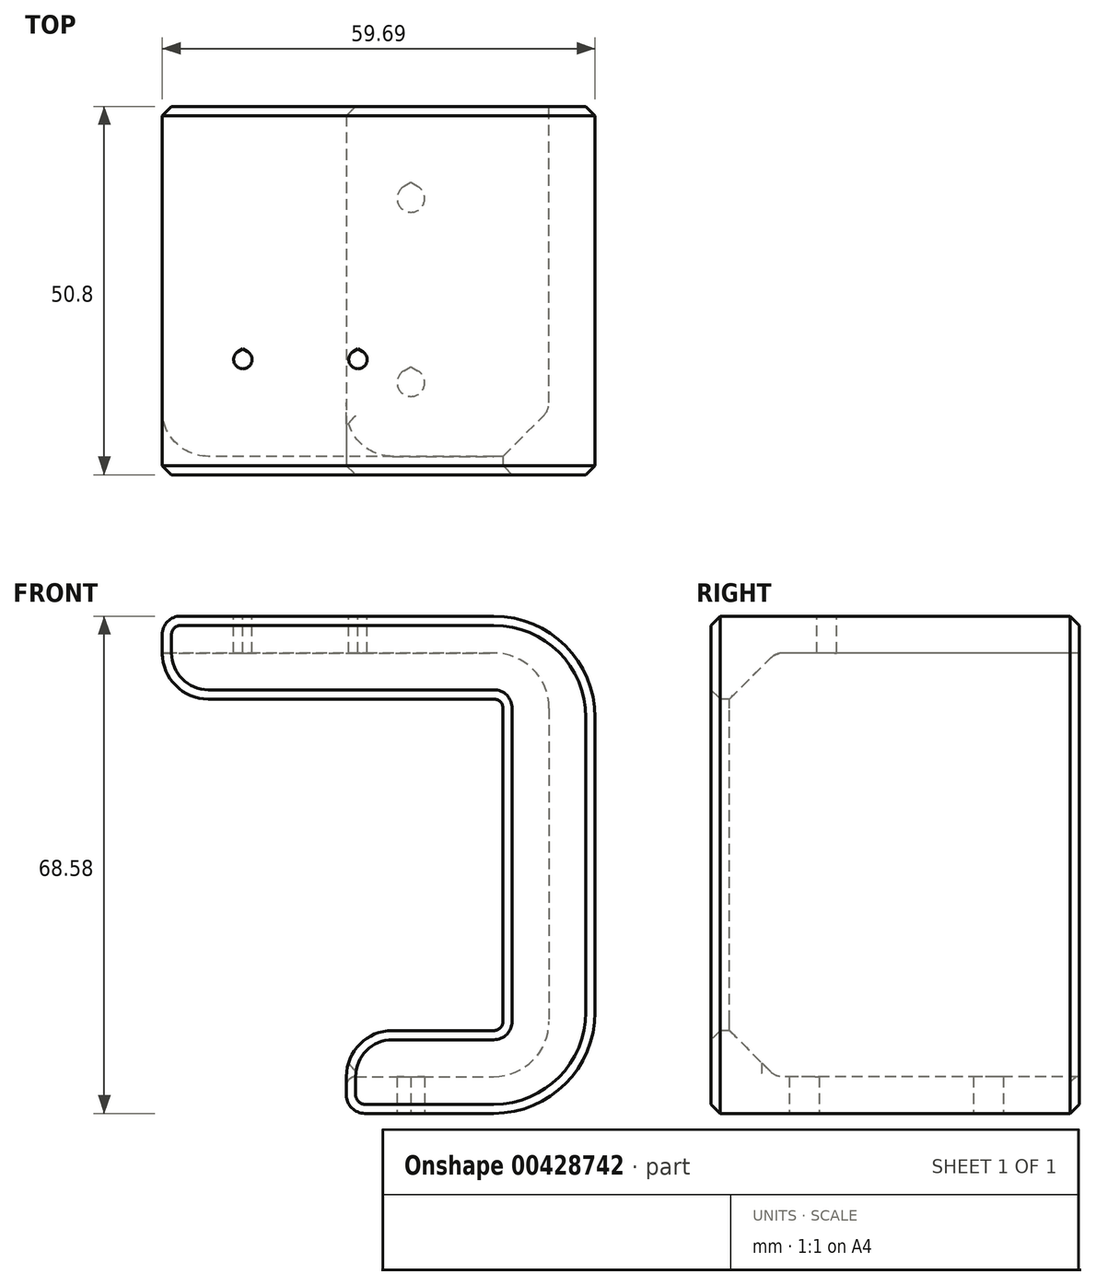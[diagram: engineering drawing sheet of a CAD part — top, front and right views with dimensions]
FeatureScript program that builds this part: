
annotation { "Feature Type Name" : "Feature", "Feature Type Description" : "" }
export const myFeature = defineFeature(function(context is Context, id is Id, definition is map)
    precondition{}
    {
        {
            var Q0;
            Q0=qCreatedBy(makeId("Top.planeOp"),FACE);
            var sketch = newSketch(context, id + "F0", { "sketchPlane" : qUnion([Q0])});
            skPoint(sketch, "E0.middle", {"position": v(0, 0) * mm});
            skArc(sketch, "E1", {"start": v(-0.95, 14.35) * mm, "mid": v(0, 10.8) * mm, "end": v(0.95, 14.35) * mm});
            skArc(sketch, "E2", {"start": v(-0.95, -11.05) * mm, "mid": v(0, -14.6) * mm, "end": v(0.95, -11.05) * mm});
            skLineSegment(sketch, "E3", {"start": v(-0.95, -11.05) * mm, "end": v(0, -10.5) * mm});
            skLineSegment(sketch, "E4", {"start": v(0, -10.5) * mm, "end": v(0.95, -11.05) * mm});
            skLineSegment(sketch, "E5", {"start": v(0.95, 14.35) * mm, "end": v(0, 14.9) * mm});
            skLineSegment(sketch, "E6", {"start": v(0, 14.9) * mm, "end": v(-0.95, 14.35) * mm});
            skLineSegment(sketch, "E7.bottom", {"start": v(-8.9, 25.4) * mm, "end": v(25.4, 25.4) * mm});
            skLineSegment(sketch, "E7.top", {"start": v(-8.9, -25.4) * mm, "end": v(25.4, -25.4) * mm});
            skLineSegment(sketch, "E7.left", {"start": v(-8.9, 25.4) * mm, "end": v(-8.9, -25.4) * mm});
            skLineSegment(sketch, "E7.right", {"start": v(25.4, 25.4) * mm, "end": v(25.4, -25.4) * mm});
            skSolve(sketch);
        }
        {
            var Q0;
            Q0 = qSketchRegion(id + "F0", true);
            extrude(context, id + "F1", {"entities" : qUnion([Q0]), "depth" : 5.08 * mm});
        }
        {
            var Q0;
            Q0=makeQuery(id+"F1.opExtrude","CAP_FACE",FACE,{"disambiguationData":[OSD([sQuery(id+"F0.wireOp",EDGE,"E1"),sQuery(id+"F0.wireOp",EDGE,"E2"),sQuery(id+"F0.wireOp",EDGE,"E3"),sQuery(id+"F0.wireOp",EDGE,"E4"),sQuery(id+"F0.wireOp",EDGE,"E5"),sQuery(id+"F0.wireOp",EDGE,"E6"),sQuery(id+"F0.wireOp",EDGE,"E7.bottom"),sQuery(id+"F0.wireOp",EDGE,"E7.top"),sQuery(id+"F0.wireOp",EDGE,"E7.left"),sQuery(id+"F0.wireOp",EDGE,"E7.right")])],"isStart":true});
            var sketch = newSketch(context, id + "F2", { "sketchPlane" : qUnion([Q0])});
            skLineSegment(sketch, "E8.bottom", {"start": v(25.4, 25.4) * mm, "end": v(19.05, 25.4) * mm});
            skLineSegment(sketch, "E8.top", {"start": v(25.4, -25.4) * mm, "end": v(19.05, -25.4) * mm});
            skLineSegment(sketch, "E8.left", {"start": v(25.4, -25.4) * mm, "end": v(25.4, 25.4) * mm});
            skLineSegment(sketch, "E8.right", {"start": v(19.05, -25.4) * mm, "end": v(19.05, 25.4) * mm});
            skSolve(sketch);
        }
        {
            var Q0;
            Q0=makeQuery(id+"F2.imprint","IMPRINT",FACE,{"disambiguationData":[TD([[makeQuery(id+"F2.imprint","IMPRINT",EDGE,{"derivedFrom":sQuery(id+"F2.wireOp",EDGE,"E8.bottom")}),-1.0]])]});
            extrude(context, id + "F3", {"entities" : qUnion([Q0]), "operationType" : NewBodyOperationType.ADD, "oppositeDirection" : true, "depth" : 68.58 * mm, "offsetDistance" : 25.4 * mm});
        }
        {
            var Q0;
            Q0=makeQuery(id+"F3.opExtrude","CAP_FACE",FACE,{"disambiguationData":[OSD([sQuery(id+"F2.wireOp",EDGE,"E8.bottom"),sQuery(id+"F2.wireOp",EDGE,"E8.top"),sQuery(id+"F2.wireOp",EDGE,"E8.left"),sQuery(id+"F2.wireOp",EDGE,"E8.right")])],"isStart":false});
            var sketch = newSketch(context, id + "F4", { "sketchPlane" : qUnion([Q0])});
            skLineSegment(sketch, "E9.bottom", {"start": v(25.4, 25.4) * mm, "end": v(-34.3, 25.4) * mm});
            skLineSegment(sketch, "E9.top", {"start": v(25.4, -25.4) * mm, "end": v(-34.3, -25.4) * mm});
            skLineSegment(sketch, "E9.left", {"start": v(25.4, 25.4) * mm, "end": v(25.4, -25.4) * mm});
            skLineSegment(sketch, "E9.right", {"start": v(-34.3, 25.4) * mm, "end": v(-34.3, -25.4) * mm});
            skSolve(sketch);
        }
        {
            var Q0;
            Q0 = qSketchRegion(id + "F4", true);
            extrude(context, id + "F5", {"entities" : qUnion([Q0]), "operationType" : NewBodyOperationType.ADD, "oppositeDirection" : true, "depth" : 5.08 * mm});
        }
        {
            var Q0;
            Q0=makeQuery(id+"F5.boolean.opBoolean","MERGE",FACE,{"derivedFrom":[makeQuery(id+"F3.opExtrude","CAP_FACE",FACE,{"disambiguationData":[OSD([sQuery(id+"F2.wireOp",EDGE,"E8.bottom"),sQuery(id+"F2.wireOp",EDGE,"E8.top"),sQuery(id+"F2.wireOp",EDGE,"E8.left"),sQuery(id+"F2.wireOp",EDGE,"E8.right")])],"isStart":false}),makeQuery(id+"F5.opExtrude","CAP_FACE",FACE,{"disambiguationData":[OSD([sQuery(id+"F4.wireOp",EDGE,"E9.bottom"),sQuery(id+"F4.wireOp",EDGE,"E9.top"),sQuery(id+"F4.wireOp",EDGE,"E9.left"),sQuery(id+"F4.wireOp",EDGE,"E9.right")])],"isStart":true})]});
            var sketch = newSketch(context, id + "F6", { "sketchPlane" : qUnion([Q0])});
            skLineSegment(sketch, "E10", {"start": v(-34.3, -9.53) * mm, "end": v(-23.18, -9.53) * mm, "construction": true});
            skLineSegment(sketch, "E11", {"start": v(-23.18, -9.53) * mm, "end": v(-7.3, -9.53) * mm, "construction": true});
            skLineSegment(sketch, "E12", {"start": v(-7.3, -9.53) * mm, "end": v(3.81, -9.53) * mm, "construction": true});
            skArc(sketch, "E13", {"start": v(-23.81, -8.43) * mm, "mid": v(-23.18, -10.8) * mm, "end": v(-22.54, -8.43) * mm});
            skArc(sketch, "E14", {"start": v(-7.94, -8.43) * mm, "mid": v(-7.3, -10.8) * mm, "end": v(-6.67, -8.43) * mm});
            skLineSegment(sketch, "E15", {"start": v(-23.81, -8.43) * mm, "end": v(-23.18, -8.06) * mm});
            skLineSegment(sketch, "E16", {"start": v(-23.18, -8.06) * mm, "end": v(-22.54, -8.43) * mm});
            skLineSegment(sketch, "E17", {"start": v(-7.94, -8.43) * mm, "end": v(-7.3, -8.06) * mm});
            skLineSegment(sketch, "E18", {"start": v(-7.3, -8.06) * mm, "end": v(-6.67, -8.43) * mm});
            skSolve(sketch);
        }
        {
            var Q0;
            Q0 = qSketchRegion(id + "F6", true);
            extrude(context, id + "F7", {"entities" : qUnion([Q0]), "operationType" : NewBodyOperationType.REMOVE, "oppositeDirection" : true, "depth" : 25.4 * mm});
        }
        {
            var Q0;
            Q0=makeQuery(id+"F5.boolean.opBoolean","MERGE",FACE,{"derivedFrom":[makeQuery(id+"F3.boolean.opBoolean","MERGE",FACE,{"derivedFrom":[makeQuery(id+"F1.opExtrude","SWEPT_FACE",FACE,{"disambiguationData":[OSD([sQuery(id+"F0.wireOp",EDGE,"E7.top")])]}),makeQuery(id+"F3.opExtrude","SWEPT_FACE",FACE,{"disambiguationData":[OSD([sQuery(id+"F2.wireOp",EDGE,"E8.bottom")])]})]}),makeQuery(id+"F5.opExtrude","SWEPT_FACE",FACE,{"disambiguationData":[OSD([sQuery(id+"F4.wireOp",EDGE,"E9.top")])]})]});
            var sketch = newSketch(context, id + "F8", { "sketchPlane" : qUnion([Q0])});
            skLineSegment(sketch, "E19", {"start": v(-34.3, 68.58) * mm, "end": v(25.4, 68.58) * mm});
            skLineSegment(sketch, "E20", {"start": v(25.4, 68.58) * mm, "end": v(25.4, 0) * mm});
            skLineSegment(sketch, "E21", {"start": v(25.4, 0) * mm, "end": v(-8.89, 0) * mm});
            skLineSegment(sketch, "E22", {"start": v(-8.9, 0) * mm, "end": v(-8.9, 11.43) * mm});
            skLineSegment(sketch, "E23", {"start": v(-8.9, 11.43) * mm, "end": v(12.7, 11.43) * mm});
            skLineSegment(sketch, "E24", {"start": v(12.7, 11.43) * mm, "end": v(12.7, 57.15) * mm});
            skLineSegment(sketch, "E25", {"start": v(12.7, 57.15) * mm, "end": v(-34.3, 57.15) * mm});
            skLineSegment(sketch, "E26", {"start": v(-34.3, 57.15) * mm, "end": v(-34.3, 68.58) * mm});
            skLineSegment(sketch, "E27", {"start": v(12.7, 57.15) * mm, "end": v(19.05, 63.5) * mm, "construction": true});
            skLineSegment(sketch, "E28", {"start": v(19.05, 5.08) * mm, "end": v(12.7, 11.43) * mm, "construction": true});
            skSolve(sketch);
        }
        {
            var Q0;
            Q0 = qSketchRegion(id + "F8", true);
            extrude(context, id + "F9", {"entities" : qUnion([Q0]), "operationType" : NewBodyOperationType.ADD, "oppositeDirection" : true, "depth" : 2.54 * mm});
        }
        {
            var Q0;
            Q0=makeQuery(id+"F3.boolean.opBoolean","INTERSECT",EDGE,{"derivedFrom":[makeQuery(id+"F1.opExtrude","CAP_FACE",FACE,{"disambiguationData":[OSD([sQuery(id+"F0.wireOp",EDGE,"E1"),sQuery(id+"F0.wireOp",EDGE,"E2"),sQuery(id+"F0.wireOp",EDGE,"E3"),sQuery(id+"F0.wireOp",EDGE,"E4"),sQuery(id+"F0.wireOp",EDGE,"E5"),sQuery(id+"F0.wireOp",EDGE,"E6"),sQuery(id+"F0.wireOp",EDGE,"E7.bottom"),sQuery(id+"F0.wireOp",EDGE,"E7.top"),sQuery(id+"F0.wireOp",EDGE,"E7.left"),sQuery(id+"F0.wireOp",EDGE,"E7.right")])],"isStart":false}),makeQuery(id+"F3.opExtrude","SWEPT_FACE",FACE,{"disambiguationData":[OSD([sQuery(id+"F2.wireOp",EDGE,"E8.right")])]})]});
            var Q1;
            Q1=makeQuery(id+"F5.boolean.opBoolean","INTERSECT",EDGE,{"derivedFrom":[makeQuery(id+"F3.opExtrude","SWEPT_FACE",FACE,{"disambiguationData":[OSD([sQuery(id+"F2.wireOp",EDGE,"E8.right")])]}),makeQuery(id+"F5.opExtrude","CAP_FACE",FACE,{"disambiguationData":[OSD([sQuery(id+"F4.wireOp",EDGE,"E9.bottom"),sQuery(id+"F4.wireOp",EDGE,"E9.top"),sQuery(id+"F4.wireOp",EDGE,"E9.left"),sQuery(id+"F4.wireOp",EDGE,"E9.right")])],"isStart":false})]});
            fillet(context, id + "F10", {"entities" : qUnion([Q0, Q1]), "radius" : 7.62 * mm, "tangentPropagation" : true, "allowEdgeOverflow" : false});
        }
        {
            var Q0;
            Q0=makeQuery(id+"FIq8xDrbzW9XsuT_1.1.F9.opExtrude","SWEPT_EDGE",EDGE,{"disambiguationData":[OSD([sQuery(id+"F8.wireOp",EDGE,"E23"),sQuery(id+"F8.wireOp",EDGE,"E24")])]});
            var Q1;
            Q1=makeQuery(id+"F9.opExtrude","SWEPT_EDGE",EDGE,{"disambiguationData":[OSD([sQuery(id+"F8.wireOp",EDGE,"E23"),sQuery(id+"F8.wireOp",EDGE,"E24")])]});
            var Q2;
            Q2=makeQuery(id+"FIq8xDrbzW9XsuT_1.1.F9.opExtrude","SWEPT_EDGE",EDGE,{"disambiguationData":[OSD([sQuery(id+"F8.wireOp",EDGE,"E24"),sQuery(id+"F8.wireOp",EDGE,"E25")])]});
            var Q3;
            Q3=makeQuery(id+"F9.opExtrude","SWEPT_EDGE",EDGE,{"disambiguationData":[OSD([sQuery(id+"F8.wireOp",EDGE,"E24"),sQuery(id+"F8.wireOp",EDGE,"E25")])]});
            fillet(context, id + "F11", {"entities" : qUnion([Q0, Q1, Q2, Q3]), "radius" : 1.27 * mm, "tangentPropagation" : true, "allowEdgeOverflow" : false});
        }
        {
            var Q0;
            Q0=makeQuery(id+"F3.opExtrude","CAP_EDGE",EDGE,{"disambiguationData":[OSD([sQuery(id+"F2.wireOp",EDGE,"E8.left")])],"isStart":false});
            var Q1;
            Q1=makeQuery(id+"F1.opExtrude","CAP_EDGE",EDGE,{"disambiguationData":[OSD([sQuery(id+"F0.wireOp",EDGE,"E7.right")])],"isStart":true});
            fillet(context, id + "F12", {"entities" : qUnion([Q0, Q1]), "radius" : 13.97 * mm, "tangentPropagation" : true, "allowEdgeOverflow" : false});
        }
        {
            var Q0;
            Q0=makeQuery(id+"F9.boolean.opBoolean","INTERSECT",EDGE,{"derivedFrom":[makeQuery(id+"F5.opExtrude","CAP_FACE",FACE,{"disambiguationData":[OSD([sQuery(id+"F4.wireOp",EDGE,"E9.bottom"),sQuery(id+"F4.wireOp",EDGE,"E9.top"),sQuery(id+"F4.wireOp",EDGE,"E9.left"),sQuery(id+"F4.wireOp",EDGE,"E9.right")])],"isStart":false}),makeQuery(id+"F9.opExtrude","CAP_FACE",FACE,{"disambiguationData":[OSD([sQuery(id+"F8.wireOp",EDGE,"E19"),sQuery(id+"F8.wireOp",EDGE,"E20"),sQuery(id+"F8.wireOp",EDGE,"E21"),sQuery(id+"F8.wireOp",EDGE,"E22"),sQuery(id+"F8.wireOp",EDGE,"E23"),sQuery(id+"F8.wireOp",EDGE,"E24"),sQuery(id+"F8.wireOp",EDGE,"E25"),sQuery(id+"F8.wireOp",EDGE,"E26")])],"isStart":false})]});
            var Q1;
            Q1=makeQuery(id+"FIq8xDrbzW9XsuT_1.1.F9.boolean.opBoolean","INTERSECT",EDGE,{"derivedFrom":[makeQuery(id+"F5.opExtrude","CAP_FACE",FACE,{"disambiguationData":[OSD([sQuery(id+"F4.wireOp",EDGE,"E9.bottom"),sQuery(id+"F4.wireOp",EDGE,"E9.top"),sQuery(id+"F4.wireOp",EDGE,"E9.left"),sQuery(id+"F4.wireOp",EDGE,"E9.right")])],"isStart":false}),makeQuery(id+"FIq8xDrbzW9XsuT_1.1.F9.opExtrude","CAP_FACE",FACE,{"disambiguationData":[OSD([sQuery(id+"F8.wireOp",EDGE,"E19"),sQuery(id+"F8.wireOp",EDGE,"E20"),sQuery(id+"F8.wireOp",EDGE,"E21"),sQuery(id+"F8.wireOp",EDGE,"E22"),sQuery(id+"F8.wireOp",EDGE,"E23"),sQuery(id+"F8.wireOp",EDGE,"E24"),sQuery(id+"F8.wireOp",EDGE,"E25"),sQuery(id+"F8.wireOp",EDGE,"E26")])],"isStart":false})]});
            chamfer(context, id + "F13", {"entities" : qUnion([Q0, Q1]), "width" : 6.35 * mm, "tangentPropagation" : true});
        }
        {
            var Q0;
            {var subQ0=makeQuery(id+"F5.opExtrude","CAP_FACE",FACE,{"disambiguationData":[OSD([sQuery(id+"F4.wireOp",EDGE,"E9.bottom"),sQuery(id+"F4.wireOp",EDGE,"E9.top"),sQuery(id+"F4.wireOp",EDGE,"E9.left"),sQuery(id+"F4.wireOp",EDGE,"E9.right")])],"isStart":false});Q0=makeQuery(id+"F13.opChamfer","BLEND_EDGE",EDGE,{"blendedFrom":[makeQuery(id+"FIq8xDrbzW9XsuT_1.1.F9.boolean.opBoolean","INTERSECT",EDGE,{"derivedFrom":[subQ0,makeQuery(id+"FIq8xDrbzW9XsuT_1.1.F9.opExtrude","CAP_FACE",FACE,{"disambiguationData":[OSD([sQuery(id+"F8.wireOp",EDGE,"E19"),sQuery(id+"F8.wireOp",EDGE,"E20"),sQuery(id+"F8.wireOp",EDGE,"E21"),sQuery(id+"F8.wireOp",EDGE,"E22"),sQuery(id+"F8.wireOp",EDGE,"E23"),sQuery(id+"F8.wireOp",EDGE,"E24"),sQuery(id+"F8.wireOp",EDGE,"E25"),sQuery(id+"F8.wireOp",EDGE,"E26")])],"isStart":false})]}),subQ0],"blendedInto":[subQ0]});}
            var Q1;
            {var subQ0=makeQuery(id+"F5.opExtrude","CAP_FACE",FACE,{"disambiguationData":[OSD([sQuery(id+"F4.wireOp",EDGE,"E9.bottom"),sQuery(id+"F4.wireOp",EDGE,"E9.top"),sQuery(id+"F4.wireOp",EDGE,"E9.left"),sQuery(id+"F4.wireOp",EDGE,"E9.right")])],"isStart":false});Q1=makeQuery(id+"F13.opChamfer","BLEND_EDGE",EDGE,{"blendedFrom":[makeQuery(id+"F9.boolean.opBoolean","INTERSECT",EDGE,{"derivedFrom":[subQ0,makeQuery(id+"F9.opExtrude","CAP_FACE",FACE,{"disambiguationData":[OSD([sQuery(id+"F8.wireOp",EDGE,"E19"),sQuery(id+"F8.wireOp",EDGE,"E20"),sQuery(id+"F8.wireOp",EDGE,"E21"),sQuery(id+"F8.wireOp",EDGE,"E22"),sQuery(id+"F8.wireOp",EDGE,"E23"),sQuery(id+"F8.wireOp",EDGE,"E24"),sQuery(id+"F8.wireOp",EDGE,"E25"),sQuery(id+"F8.wireOp",EDGE,"E26")])],"isStart":false})]}),subQ0],"blendedInto":[subQ0]});}
            fillet(context, id + "F14", {"entities" : qUnion([Q0, Q1]), "radius" : 2.54 * mm, "tangentPropagation" : true, "allowEdgeOverflow" : false});
        }
        {
            var Q0;
            Q0=makeQuery(id+"FIq8xDrbzW9XsuT_1.1.F9.opExtrude","SWEPT_EDGE",EDGE,{"disambiguationData":[OSD([sQuery(id+"F8.wireOp",EDGE,"E22"),sQuery(id+"F8.wireOp",EDGE,"E23")])]});
            var Q1;
            Q1=makeQuery(id+"F9.opExtrude","SWEPT_EDGE",EDGE,{"disambiguationData":[OSD([sQuery(id+"F8.wireOp",EDGE,"E22"),sQuery(id+"F8.wireOp",EDGE,"E23")])]});
            var Q2;
            Q2=makeQuery(id+"F9.opExtrude","SWEPT_EDGE",EDGE,{"disambiguationData":[OSD([sQuery(id+"F8.wireOp",EDGE,"E25"),sQuery(id+"F8.wireOp",EDGE,"E26")])]});
            var Q3;
            Q3=makeQuery(id+"FIq8xDrbzW9XsuT_1.1.F9.opExtrude","SWEPT_EDGE",EDGE,{"disambiguationData":[OSD([sQuery(id+"F8.wireOp",EDGE,"E25"),sQuery(id+"F8.wireOp",EDGE,"E26")])]});
            fillet(context, id + "F15", {"entities" : qUnion([Q0, Q1, Q2, Q3]), "radius" : 6.35 * mm, "tangentPropagation" : true, "allowEdgeOverflow" : false});
        }
        {
            var Q0;
            Q0=makeQuery(id+"F1.opExtrude","CAP_EDGE",EDGE,{"disambiguationData":[OSD([sQuery(id+"F0.wireOp",EDGE,"E7.left")])],"isStart":true});
            var Q1;
            Q1=makeQuery(id+"F5.opExtrude","CAP_EDGE",EDGE,{"disambiguationData":[OSD([sQuery(id+"F4.wireOp",EDGE,"E9.right")])],"isStart":true});
            fillet(context, id + "F16", {"entities" : qUnion([Q0, Q1]), "radius" : 2.54 * mm, "tangentPropagation" : true, "allowEdgeOverflow" : false});
        }
        {
            var Q0;
            Q0=makeQuery(id+"F5.boolean.opBoolean","MERGE",EDGE,{"derivedFrom":[makeQuery(id+"F3.opExtrude","CAP_EDGE",EDGE,{"disambiguationData":[OSD([sQuery(id+"F2.wireOp",EDGE,"E8.top")])],"isStart":false}),makeQuery(id+"F5.opExtrude","CAP_EDGE",EDGE,{"disambiguationData":[OSD([sQuery(id+"F4.wireOp",EDGE,"E9.bottom")])],"isStart":true})]});
            var Q1;
            Q1=makeQuery(id+"F5.boolean.opBoolean","MERGE",EDGE,{"derivedFrom":[makeQuery(id+"F3.opExtrude","CAP_EDGE",EDGE,{"disambiguationData":[OSD([sQuery(id+"F2.wireOp",EDGE,"E8.bottom")])],"isStart":false}),makeQuery(id+"F5.opExtrude","CAP_EDGE",EDGE,{"disambiguationData":[OSD([sQuery(id+"F4.wireOp",EDGE,"E9.top")])],"isStart":true})]});
            chamfer(context, id + "F17", {"entities" : qUnion([Q0, Q1]), "width" : 1.27 * mm, "tangentPropagation" : true});
        }
        {
            var Q0;
            Q0=makeQuery(id+"F1.opExtrude","CAP_EDGE",EDGE,{"disambiguationData":[OSD([sQuery(id+"F0.wireOp",EDGE,"E7.left")])],"isStart":false});
            fillet(context, id + "F18", {"entities" : qUnion([Q0]), "radius" : 1.27 * mm, "tangentPropagation" : true, "allowEdgeOverflow" : false});
        }
    });
